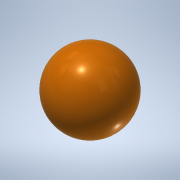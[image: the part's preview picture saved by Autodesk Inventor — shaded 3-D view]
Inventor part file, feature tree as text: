
AUTODESK INVENTOR PART (.ipt)
format: ipt  version: 2020.2 (Build 242310000, 310)  size: 183,296 bytes
history: native  units: mm
features: other x1, revolve x1, sketch x1
ambient origin geometry x8: Origin, YZ Plane, XZ Plane, XY Plane, X Axis, Y Axis, Z Axis, Center Point
bodies: Volumenkörper1 (feature_tree)
feature tree (3):
  other  "Golfball"
  revolve  "Umdrehung1"
  sketch  "Skizze1"  dims[d0=42.67mm d2=90.0deg]
